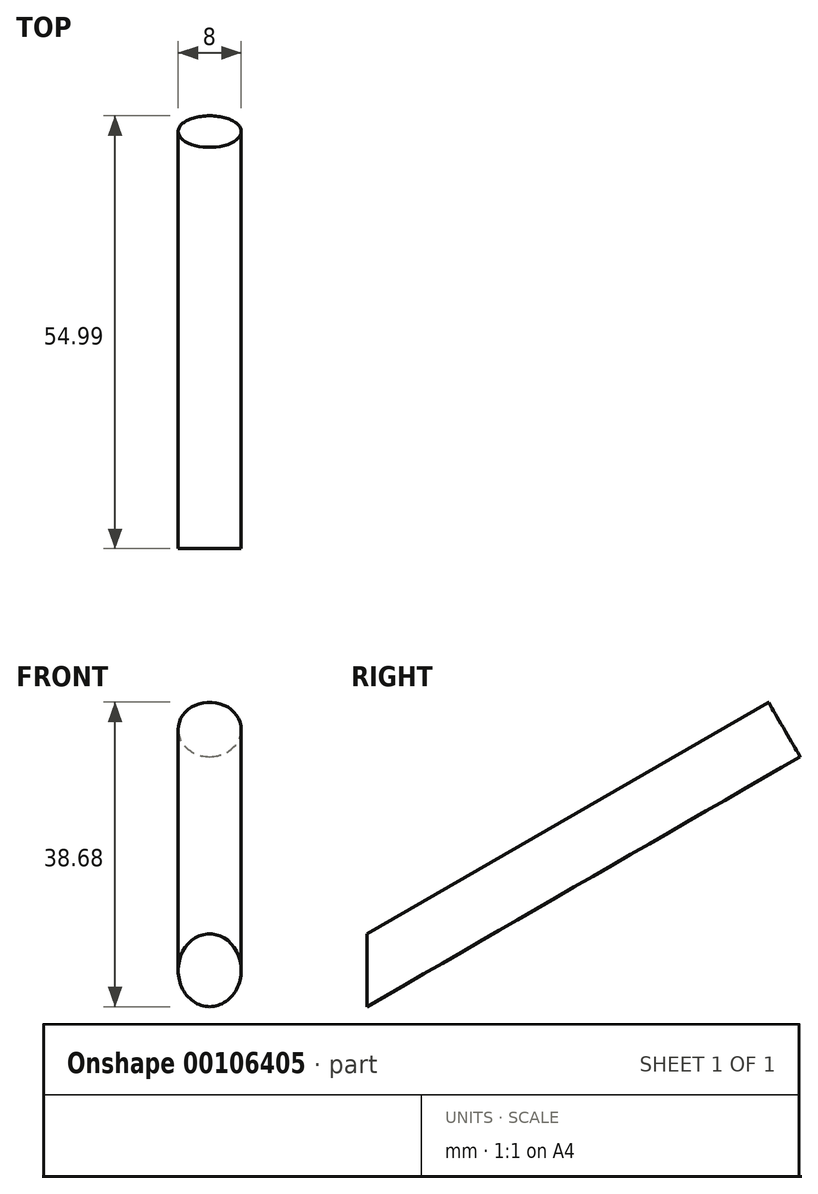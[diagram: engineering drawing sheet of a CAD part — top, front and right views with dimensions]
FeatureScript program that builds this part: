
annotation { "Feature Type Name" : "Feature", "Feature Type Description" : "" }
export const myFeature = defineFeature(function(context is Context, id is Id, definition is map)
    precondition{}
    {
        {
            var Q0;
            Q0=qCreatedBy(makeId("Front.planeOp"),FACE);
            var sketch = newSketch(context, id + "F0", { "sketchPlane" : qUnion([Q0])});
            skCircle(sketch, "E0", {"center": v(0, 4) * mm, "radius": 4 * mm});
            skLineSegment(sketch, "E1", {"start": v(0, 4) * mm, "end": v(0, 0) * mm, "construction": true});
            skSolve(sketch);
        }
        {
            var Q0;
            Q0=makeQuery(id+"F0.imprint","IMPRINT",FACE,{"disambiguationData":[TD([[makeQuery(id+"F0.imprint","IMPRINT",EDGE,{"derivedFrom":sQuery(id+"F0.wireOp",EDGE,"E0")}),1.0]])]});
            extrude(context, id + "F1", {"entities" : qUnion([Q0]), "oppositeDirection" : true, "depth" : 63.5 * mm});
        }
        {
            var Q0;
            Q0=qCreatedBy(makeId("Top.planeOp"),FACE);
            var sketch = newSketch(context, id + "F2", { "sketchPlane" : qUnion([Q0])});
            skLineSegment(sketch, "E2", {"start": v(-18.7, 0) * mm, "end": v(24.46, 0) * mm});
            skSolve(sketch);
        }
        {
            var Q0;
            Q0=makeQuery(id+"F1.opExtrude","SWEPT_BODY",BODY,{"disambiguationData":[OSD([sQuery(id+"F0.wireOp",EDGE,"E0")])]});
            var Q1;
            Q1=sQuery(id+"F2.wireOp",EDGE,"E2");
            transform(context, id + "F3", {"entities" : qUnion([Q0]), "transformType" : TransformType.ROTATION, "transformAxis" : qUnion([Q1]), "angle" : 30 * degree, "makeCopy" : false});
        }
        {
            var Q0;
            Q0=qCreatedBy(makeId("Front.planeOp"),FACE);
            var sketch = newSketch(context, id + "F4", { "sketchPlane" : qUnion([Q0])});
            skLineSegment(sketch, "E3.bottom", {"start": v(10, -10) * mm, "end": v(-10, -10) * mm});
            skLineSegment(sketch, "E3.top", {"start": v(10, 10) * mm, "end": v(-10, 10) * mm});
            skLineSegment(sketch, "E3.left", {"start": v(10, -10) * mm, "end": v(10, 10) * mm});
            skLineSegment(sketch, "E3.right", {"start": v(-10, -10) * mm, "end": v(-10, 10) * mm});
            skPoint(sketch, "E3.middle", {"position": v(0, 0) * mm});
            skSolve(sketch);
        }
        {
            var Q0;
            Q0=makeQuery(id+"F4.imprint","IMPRINT",FACE,{"disambiguationData":[TD([[makeQuery(id+"F4.imprint","IMPRINT",EDGE,{"derivedFrom":sQuery(id+"F4.wireOp",EDGE,"E3.bottom")}),-1.0]])]});
            extrude(context, id + "F5", {"entities" : qUnion([Q0]), "operationType" : NewBodyOperationType.REMOVE, "endBound" : BoundingType.THROUGH_ALL, "depth" : 25 * mm});
        }
    });
